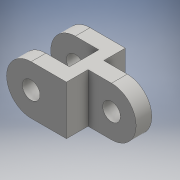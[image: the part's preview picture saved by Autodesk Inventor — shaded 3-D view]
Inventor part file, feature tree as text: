
AUTODESK INVENTOR PART (.ipt)
format: ipt  version: 2016 (Build 200138000, 138)  size: 135,680 bytes
history: native  units: mm
features: sketch x2, extrude x1, fillet x1, hole x1
ambient origin geometry x8: Origin, YZ Plane, XZ Plane, XY Plane, X Axis, Y Axis, Z Axis, Center Point
bodies: Solid1 (feature_tree)
feature tree (5):
  extrude  "Extrusion1"  Depth=15.0mm
  fillet  "Fillet1"  Radius=60.0mm
  hole  "Hole1"  [1 undecoded]
  sketch  "Sketch1"  dims[d0=15.0mm d1=15.0mm d2=60.0mm]
  sketch  "Sketch2"  dims[d3=12.0mm d4=61.0mm d5=22.0mm d6=22.0mm d7=49.0mm d8=43.628319mm d9=1.561947mm d10=50.0mm d11=0.0mm d12=25.0mm d13=18.0mm d14=6.0mm d15=4.0mm d16=2.0mm d17=90.0deg d18=8.0mm d19=20.594885mm]
note: 1 required parameter value undecoded (feature->parameter linkage not recoverable at this tier; creation-order binding heuristic only, values carry confidence <= 0.55)
